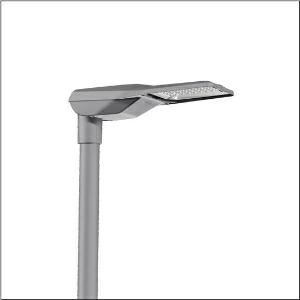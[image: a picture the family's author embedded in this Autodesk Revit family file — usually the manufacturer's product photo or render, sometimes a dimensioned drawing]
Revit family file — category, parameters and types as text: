
# Revit family: streetlight_sl_21_iq_mini___st1_0a_5xe2d41g08gb_82d1
name_source: partatom
category: Lighting Fixtures
units: mm (PartAtom-declared; Revit-internal decimal feet)

## family parameters
Cut with Voids When Loaded = No
Host = Face
Light Source = No
Part Type = Normal
Room Calculation Point = No
Round Connector Dimension = Use Diameter
Shared = No

## types (1)
- --- (1 x LED, 5920 lm, 37.1 W, 4000K)
    Apparent Load = 37 VA
    CIE Flux Codes = 37 72 97 100 100
    Color Rendering = 70
    Color Temperature = 4000K
    Default Elevation = 1800 mm
    Description = Streetlight SL 21 iQ mini, mast luminaire, primary light control with lens, of PMMA, primary optical cover: cover, of toughened safety glass, transparent, light distribution: ST1.0a, light emission: direct distribution, primary light characteristic: asymmetric, installation type: post-top, side-entry, LED, High Power LED, rated luminous flux: 5.920lm, luminous efficacy: 160lm/W, light colour: 740, colour temperature: 4000K, control: Street-Remote, Auto-Match, Temp-Guard, Lumen-Switch, Night-Set, Smart-Wire, Light-Fading, Desk-Remote (wireless, voltage-free reading and setting of iQ features in the workshop via application-optimized NFC function/RFID function), optimised constant luminous flux control (CLO 2.0), presetting dimming linear, mains connection: 220..240V, AC, 50/60Hz, start of lifetime: 37W, end of service life: 39W, reduction: 18W, luminaire housing, of diecast aluminium, powder-coated, Siteco® metallic grey (DB 702S), corrosivity category C5 mid according to DIN EN ISO 12944, please order mast flange separately, inclination adjustable: 0°, 5°, 10°, 15°, sealing non-destructively replaceable, multi-level sealing system, length: 628mm, width: 235mm, height: 110mm, mast flange for spigot size: 42mm (side-entry): 5XC10008XM4, 60/48mm (side-entry/post-top): 5XC10108XM2, 76/60mm (side-entry/post-top): 5XC10108XM1, protection rating (complete): IP66, insulation class (complete): insulation class II (safety insulation), certification: CE, ENEC, ENEC+, VDE, impact resistance: IK09, permissible operating ambient temperature for outdoor applications: -40..+50°C, standard-compliant lighting for roads and squares, packaging unit: 1 piece

Light Distribution: ST1.0a
    Height = 110 mm
    Lamp = 1 x LED
    Lamp Light Flux = 5920 lm
    Lamp Power = 37.1 W
    Lamp count = 1
    Length = 625 mm
    Luminous efficacy = 160 lm/W
    Manufacturer = Siteco
    ModVariant = No
    Model = 5XE2D41G08GB
    Number of Poles = 1
    OnlyDefault = Yes
    Power Factor = 1
    Product Name = Streetlight SL 21 iQ mini | ST1.0a
    Product group = mast luminaire | pylon top
    ProductGroupID = 6100
    Protection Class = Protection class II
    Protection Degree = IP 66
    RLX_Detail_Level = 1
    RLX_Emergency_Light_Flux = 0 lm
    RLX_Emergency_Type = 0
    RLX_Emergency_Type_DB = No
    RlxData = <blob elided: 91781 chars, md5=eb802acd>
    Socket = socket
    Standby Power = 0 W
    System Light Flux = 5920 lm
    System Power = 37 W
    Type Comments = factory setting: luminous flux: 100 % | dim-lin: 254 | 385 mA
    Type Image = l_1003519.jpg
    URL = http://relux.com
    VarID = @adj_140899
    Voltage = 0 V
    Weight = 0.00 kg
    Width = 234 mm

## geometry (parser evidence)
native form markers: Blend x4, Sweep x11
no freeform markers — native parametric forms only
